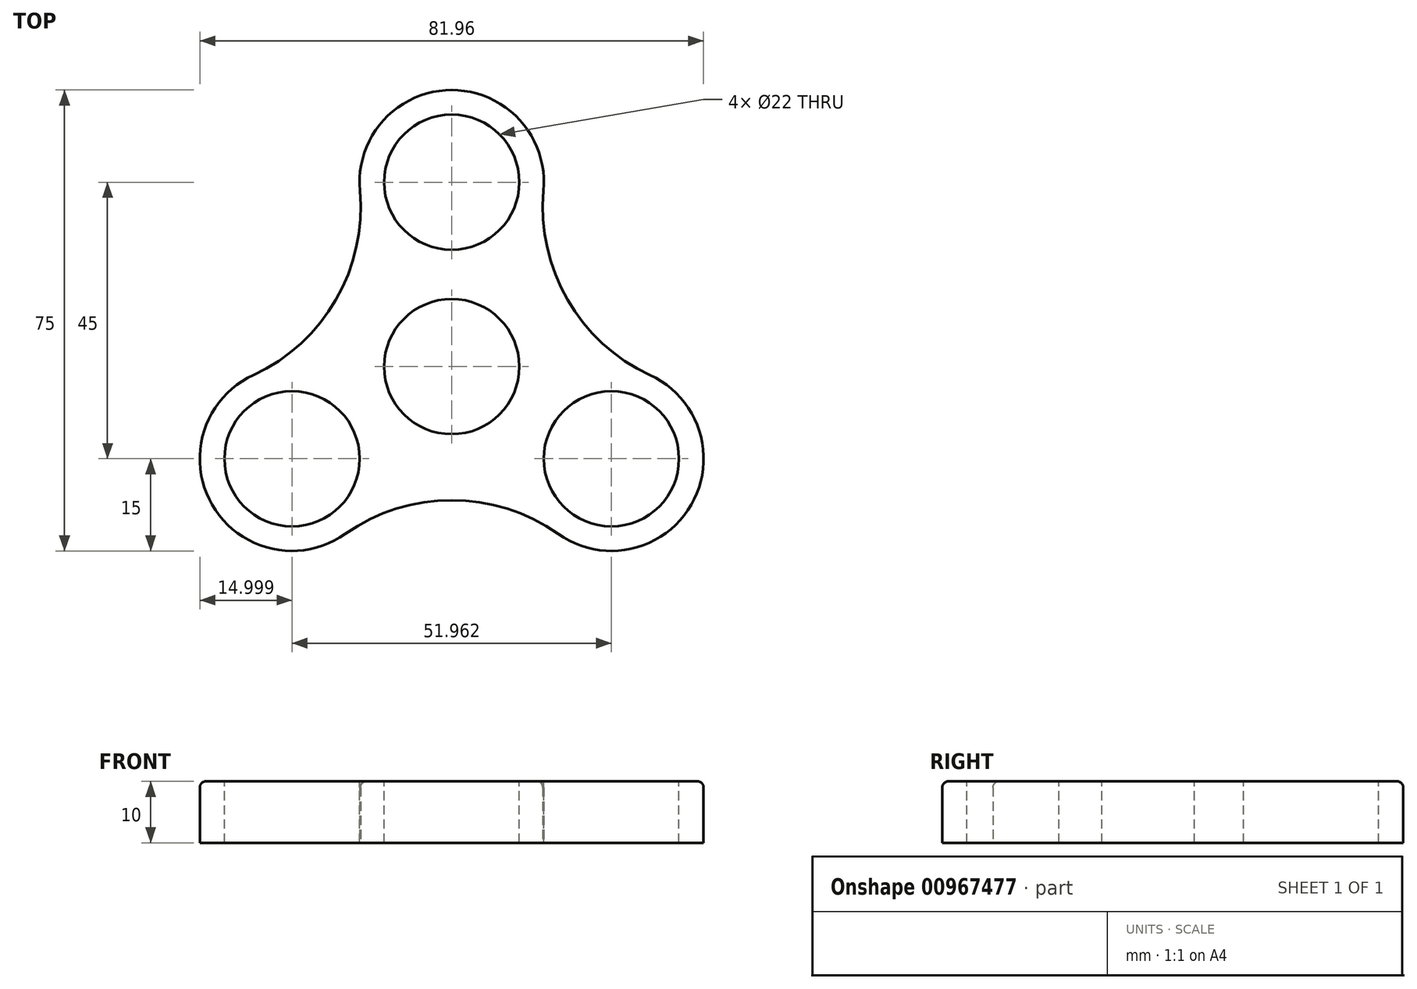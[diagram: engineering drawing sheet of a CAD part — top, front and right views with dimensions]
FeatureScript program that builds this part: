
annotation { "Feature Type Name" : "Feature", "Feature Type Description" : "" }
export const myFeature = defineFeature(function(context is Context, id is Id, definition is map)
    precondition{}
    {
        {
            var Q0;
            Q0=qCreatedBy(makeId("Top.planeOp"),FACE);
            var sketch = newSketch(context, id + "F0", { "sketchPlane" : qUnion([Q0])});
            skArc(sketch, "E0", {"start": v(14.94, 28.62) * mm, "mid": v(0, 45) * mm, "end": v(-14.94, 28.62) * mm});
            skArc(sketch, "E1.1.0", {"start": v(17.32, -27.25) * mm, "mid": v(38.97, -22.5) * mm, "end": v(32.26, -1.38) * mm});
            skArc(sketch, "E1.2.0", {"start": v(-32.26, -1.38) * mm, "mid": v(-38.97, -22.5) * mm, "end": v(-17.32, -27.25) * mm});
            skPoint(sketch, "E1.center", {"position": v(0, 0) * mm});
            skLineSegment(sketch, "E1.anchor2", {"start": v(0, 0) * mm, "end": v(-25.98, -15) * mm, "construction": true});
            skArc(sketch, "E2", {"start": v(14.94, 28.62) * mm, "mid": v(18.83, 10.87) * mm, "end": v(32.26, -1.38) * mm});
            skArc(sketch, "E3.1.0", {"start": v(-32.26, -1.38) * mm, "mid": v(-18.83, 10.87) * mm, "end": v(-14.94, 28.62) * mm});
            skArc(sketch, "E3.2.0", {"start": v(17.32, -27.25) * mm, "mid": v(0, -21.74) * mm, "end": v(-17.32, -27.25) * mm});
            skSolve(sketch);
        }
        {
            var Q0;
            Q0 = qSketchRegion(id + "F0", true);
            extrude(context, id + "F1", {"entities" : qUnion([Q0]), "depth" : 10 * mm, "offsetDistance" : 25 * mm});
        }
        {
            var Q0;
            Q0=makeQuery(id+"F1.opExtrude","CAP_FACE",FACE,{"disambiguationData":[OSD([sQuery(id+"F0.wireOp",EDGE,"E0"),sQuery(id+"F0.wireOp",EDGE,"E1.1.0"),sQuery(id+"F0.wireOp",EDGE,"E1.2.0"),sQuery(id+"F0.wireOp",EDGE,"E2"),sQuery(id+"F0.wireOp",EDGE,"E3.1.0"),sQuery(id+"F0.wireOp",EDGE,"E3.2.0")])],"isStart":false});
            var sketch = newSketch(context, id + "F2", { "sketchPlane" : qUnion([Q0])});
            skCircle(sketch, "E4", {"center": v(0, 30) * mm, "radius": 11 * mm});
            skCircle(sketch, "E5", {"center": v(25.98, -15) * mm, "radius": 11 * mm});
            skCircle(sketch, "E6", {"center": v(-25.98, -15) * mm, "radius": 11 * mm});
            skCircle(sketch, "E7", {"center": v(0, 0) * mm, "radius": 11 * mm});
            skSolve(sketch);
        }
        {
            var Q0;
            Q0=makeQuery(id+"F2.imprint","IMPRINT",FACE,{"disambiguationData":[TD([[makeQuery(id+"F2.imprint","IMPRINT",EDGE,{"derivedFrom":sQuery(id+"F2.wireOp",EDGE,"E6")}),1.0]])]});
            var Q1;
            Q1=makeQuery(id+"F2.imprint","IMPRINT",FACE,{"disambiguationData":[TD([[makeQuery(id+"F2.imprint","IMPRINT",EDGE,{"derivedFrom":sQuery(id+"F2.wireOp",EDGE,"E7")}),1.0]])]});
            var Q2;
            Q2=makeQuery(id+"F2.imprint","IMPRINT",FACE,{"disambiguationData":[TD([[makeQuery(id+"F2.imprint","IMPRINT",EDGE,{"derivedFrom":sQuery(id+"F2.wireOp",EDGE,"E4")}),1.0]])]});
            var Q3;
            Q3=makeQuery(id+"F2.imprint","IMPRINT",FACE,{"disambiguationData":[TD([[makeQuery(id+"F2.imprint","IMPRINT",EDGE,{"derivedFrom":sQuery(id+"F2.wireOp",EDGE,"E5")}),1.0]])]});
            extrude(context, id + "F3", {"entities" : qUnion([Q0, Q1, Q2, Q3]), "operationType" : NewBodyOperationType.REMOVE, "endBound" : BoundingType.THROUGH_ALL, "oppositeDirection" : true, "depth" : 25 * mm, "offsetDistance" : 25 * mm});
        }
        {
            var Q0;
            Q0=makeQuery(id+"F1.opExtrude","CAP_EDGE",EDGE,{"disambiguationData":[OSD([sQuery(id+"F0.wireOp",EDGE,"E3.2.0")])],"isStart":false});
            fillet(context, id + "F4", {"entities" : qUnion([Q0]), "radius" : 1 * mm, "tangentPropagation" : true, "allowEdgeOverflow" : false});
        }
    });
